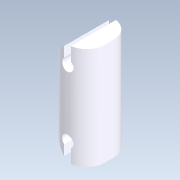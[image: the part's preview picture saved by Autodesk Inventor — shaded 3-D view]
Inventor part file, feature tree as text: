
AUTODESK INVENTOR PART (.ipt)
format: ipt  version: 2020.2 (Build 242310000, 310)  size: 163,840 bytes
history: native  units: mm
features: extrude x3, sketch x3, fillet x1
ambient origin geometry x8: Origin, YZ Plane, XZ Plane, XY Plane, X Axis, Y Axis, Z Axis, Center Point
bodies: Solid1 (feature_tree)
feature tree (7):
  extrude  "Extrusion1"  Depth=45.0mm
  extrude  "Extrusion2"  Depth=17.0mm
  fillet  "Fillet1"  Radius=17.0mm
  extrude  "Extrusion4"  TaperAngle=0.0deg  [1 undecoded]
  sketch  "Sketch1"  dims[d1=2.5mm d2=45.0mm]
  sketch  "Sketch2"  dims[d3=5.0mm d5=17.0mm d9=17.0mm]
  sketch  "Sketch4"  dims[d10=2.5mm d11=0.0mm d12=135.0deg d13=135.0deg d14=20.0mm d15=0.0mm d16=8.0mm d17=5.0mm d18=1.5mm d19=3.0mm d20=8.0mm d21=1.5mm d22=1.5mm d23=5.0mm d24=0.0mm d25=0.0mm d26=8.0mm d31=2.0mm d32=2.0mm d33=0.0mm d34=0.0mm]
note: 1 required parameter value undecoded (feature->parameter linkage not recoverable at this tier; creation-order binding heuristic only, values carry confidence <= 0.55)
